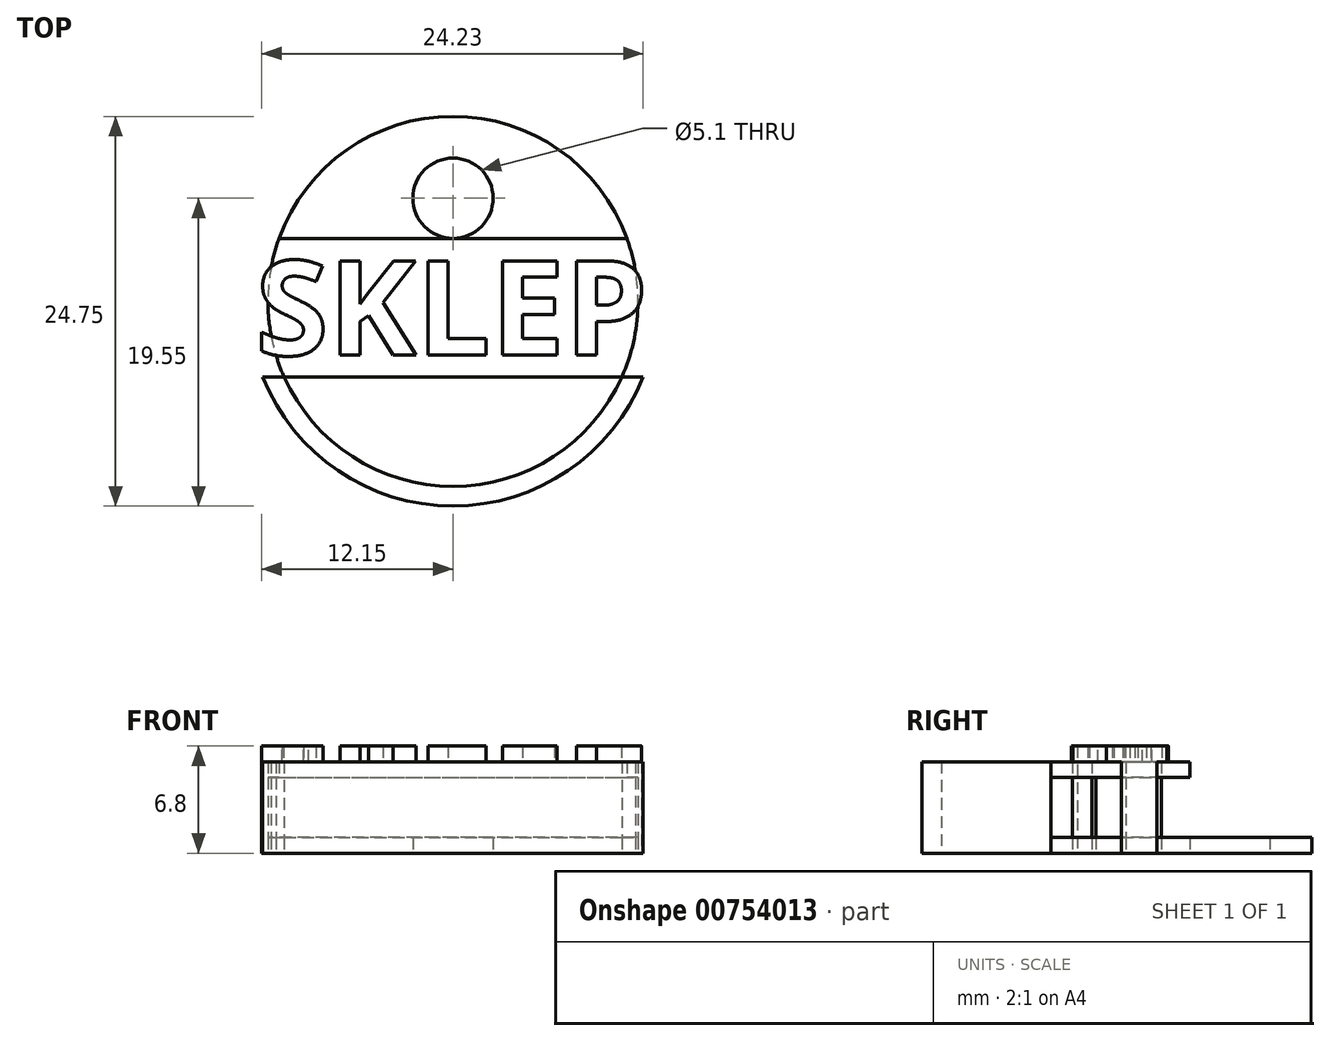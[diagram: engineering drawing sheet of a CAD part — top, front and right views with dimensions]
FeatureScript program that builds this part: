
annotation { "Feature Type Name" : "Feature", "Feature Type Description" : "" }
export const myFeature = defineFeature(function(context is Context, id is Id, definition is map)
    precondition{}
    {
        {
            var Q0;
            Q0=qCreatedBy(makeId("Top.planeOp"),FACE);
            var sketch = newSketch(context, id + "F0", { "sketchPlane" : qUnion([Q0])});
            skCircle(sketch, "E0", {"center": v(0, 0) * mm, "radius": 13 * mm});
            skLineSegment(sketch, "E1", {"start": v(-12.08, -4.8) * mm, "end": v(12.08, -4.8) * mm});
            skCircle(sketch, "E2", {"center": v(0, 6.55) * mm, "radius": 2.55 * mm});
            skCircle(sketch, "E3", {"center": v(0, 0) * mm, "radius": 11.75 * mm});
            skLineSegment(sketch, "E4", {"start": v(0, 4) * mm, "end": v(-11.05, 4) * mm});
            skLineSegment(sketch, "E5", {"start": v(0, 4) * mm, "end": v(11.05, 4) * mm});
            skText(sketch, "E6", { "text": "SKLEP", "fontName": "OpenSans-Bold.ttf"});
            const initialGuessF0  = {"E6": [-0.01254, -0.00342, 1, 0, 0.00604]};
            skSetInitialGuess(sketch, initialGuessF0);
            skSolve(sketch);
        }
        {
            var Q0;
            {var subQ0=sQuery(id+"F0.wireOp",EDGE,"E4");Q0=makeQuery(id+"F0.imprint","IMPRINT",FACE,{"disambiguationData":[TD([[makeQuery(id+"F0.imprint","IMPRINT",EDGE,{"derivedFrom":subQ0}),1.0]])]});}
            var Q1;
            {var subQ0=sQuery(id+"F0.wireOp",EDGE,"E1");var subQ1=sQuery(id+"F0.wireOp",EDGE,"E0");var subQ5=makeQuery(id+"F0.imprint","INTERSECT",VERTEX,{"disambiguationData":[OD(0.0)],"derivedFrom":[subQ1,subQ0]});Q1=makeQuery(id+"F0.imprint","IMPRINT",FACE,{"disambiguationData":[TD([[makeQuery(id+"F0.imprint","IMPRINT",EDGE,{"disambiguationData":[TD([[subQ5,1.0]])],"derivedFrom":subQ1}),1.0]])]});}
            var Q2;
            Q2=makeQuery(id+"F0.imprint","IMPRINT",FACE,{"disambiguationData":[TD([[makeQuery(id+"F0.imprint","IMPRINT",EDGE,{"derivedFrom":sQuery(id+"F0.wireOp",EDGE,"E6.sketch_text.stroke-59")}),1.0]])]});
            var Q3;
            {var subQ0=sQuery(id+"F0.wireOp",EDGE,"E6.sketch_text.stroke-5");Q3=makeQuery(id+"F0.imprint","IMPRINT",FACE,{"disambiguationData":[TD([[makeQuery(id+"F0.imprint","IMPRINT",EDGE,{"derivedFrom":subQ0}),1.0]])]});}
            extrude(context, id + "F1", {"entities" : qUnion([Q0, Q1, Q2, Q3]), "depth" : 5.8 * mm, "offsetDistance" : 25 * mm});
        }
        {
            var Q0;
            Q0=makeQuery(id+"F0.imprint","IMPRINT",FACE,{"disambiguationData":[TD([[makeQuery(id+"F0.imprint","IMPRINT",EDGE,{"derivedFrom":sQuery(id+"F0.wireOp",EDGE,"E6.sketch_text.stroke-41")}),-1.0]])]});
            var Q1;
            Q1=makeQuery(id+"F0.imprint","IMPRINT",FACE,{"disambiguationData":[TD([[makeQuery(id+"F0.imprint","IMPRINT",EDGE,{"derivedFrom":sQuery(id+"F0.wireOp",EDGE,"E6.sketch_text.stroke-47")}),-1.0]])]});
            var Q2;
            Q2=makeQuery(id+"F0.imprint","IMPRINT",FACE,{"disambiguationData":[TD([[makeQuery(id+"F0.imprint","IMPRINT",EDGE,{"derivedFrom":sQuery(id+"F0.wireOp",EDGE,"E6.sketch_text.stroke-59")}),-1.0]])]});
            var Q3;
            Q3=makeQuery(id+"F0.imprint","IMPRINT",FACE,{"disambiguationData":[TD([[makeQuery(id+"F0.imprint","IMPRINT",EDGE,{"derivedFrom":sQuery(id+"F0.wireOp",EDGE,"E6.sketch_text.stroke-28")}),-1.0]])]});
            var Q4;
            Q4=makeQuery(id+"F0.imprint","IMPRINT",FACE,{"disambiguationData":[TD([[makeQuery(id+"F0.imprint","IMPRINT",EDGE,{"derivedFrom":sQuery(id+"F0.wireOp",EDGE,"E6.sketch_text.stroke-0")}),-1.0]])]});
            var Q5;
            {var subQ5=sQuery(id+"F0.wireOp",EDGE,"E6.sketch_text.stroke-3");Q5=makeQuery(id+"F0.imprint","IMPRINT",FACE,{"disambiguationData":[TD([[makeQuery(id+"F0.imprint","IMPRINT",EDGE,{"derivedFrom":subQ5}),-1.0]])]});}
            var Q6;
            {var subQ1=sQuery(id+"F0.wireOp",EDGE,"E6.sketch_text.stroke-13");Q6=makeQuery(id+"F0.imprint","IMPRINT",FACE,{"disambiguationData":[TD([[makeQuery(id+"F0.imprint","IMPRINT",EDGE,{"derivedFrom":subQ1}),-1.0]])]});}
            var Q7;
            {var subQ5=sQuery(id+"F0.wireOp",EDGE,"E6.sketch_text.stroke-74");Q7=makeQuery(id+"F0.imprint","IMPRINT",FACE,{"disambiguationData":[TD([[makeQuery(id+"F0.imprint","IMPRINT",EDGE,{"derivedFrom":subQ5}),-1.0]])]});}
            extrude(context, id + "F2", {"entities" : qUnion([Q0, Q1, Q2, Q3, Q4, Q5, Q6, Q7]), "operationType" : NewBodyOperationType.ADD, "depth" : 6.8 * mm, "offsetDistance" : 25 * mm});
        }
        {
            var Q0;
            {var subQ0=sQuery(id+"F0.wireOp",EDGE,"E4");Q0=makeQuery(id+"F0.imprint","IMPRINT",FACE,{"disambiguationData":[TD([[makeQuery(id+"F0.imprint","IMPRINT",EDGE,{"derivedFrom":subQ0}),1.0]])]});}
            var Q1;
            Q1=makeQuery(id+"F0.imprint","IMPRINT",FACE,{"disambiguationData":[TD([[makeQuery(id+"F0.imprint","IMPRINT",EDGE,{"derivedFrom":sQuery(id+"F0.wireOp",EDGE,"E6.sketch_text.stroke-0")}),-1.0]])]});
            var Q2;
            Q2=makeQuery(id+"F0.imprint","IMPRINT",FACE,{"disambiguationData":[TD([[makeQuery(id+"F0.imprint","IMPRINT",EDGE,{"derivedFrom":sQuery(id+"F0.wireOp",EDGE,"E6.sketch_text.stroke-28")}),-1.0]])]});
            var Q3;
            Q3=makeQuery(id+"F0.imprint","IMPRINT",FACE,{"disambiguationData":[TD([[makeQuery(id+"F0.imprint","IMPRINT",EDGE,{"derivedFrom":sQuery(id+"F0.wireOp",EDGE,"E6.sketch_text.stroke-41")}),-1.0]])]});
            var Q4;
            Q4=makeQuery(id+"F0.imprint","IMPRINT",FACE,{"disambiguationData":[TD([[makeQuery(id+"F0.imprint","IMPRINT",EDGE,{"derivedFrom":sQuery(id+"F0.wireOp",EDGE,"E6.sketch_text.stroke-47")}),-1.0]])]});
            var Q5;
            Q5=makeQuery(id+"F0.imprint","IMPRINT",FACE,{"disambiguationData":[TD([[makeQuery(id+"F0.imprint","IMPRINT",EDGE,{"derivedFrom":sQuery(id+"F0.wireOp",EDGE,"E6.sketch_text.stroke-59")}),-1.0]])]});
            var Q6;
            Q6=makeQuery(id+"F0.imprint","IMPRINT",FACE,{"disambiguationData":[TD([[makeQuery(id+"F0.imprint","IMPRINT",EDGE,{"derivedFrom":sQuery(id+"F0.wireOp",EDGE,"E6.sketch_text.stroke-59")}),1.0]])]});
            var Q7;
            {var subQ0=sQuery(id+"F0.wireOp",EDGE,"E6.sketch_text.stroke-5");Q7=makeQuery(id+"F0.imprint","IMPRINT",FACE,{"disambiguationData":[TD([[makeQuery(id+"F0.imprint","IMPRINT",EDGE,{"derivedFrom":subQ0}),1.0]])]});}
            extrude(context, id + "F3", {"entities" : qUnion([Q0, Q1, Q2, Q3, Q4, Q5, Q6, Q7]), "operationType" : NewBodyOperationType.REMOVE, "depth" : 4.8 * mm, "offsetDistance" : 25 * mm});
        }
        {
            var Q0;
            Q0=makeQuery(id+"F0.imprint","IMPRINT",FACE,{"disambiguationData":[TD([[makeQuery(id+"F0.imprint","IMPRINT",EDGE,{"derivedFrom":sQuery(id+"F0.wireOp",EDGE,"E2")}),-1.0]])]});
            var Q1;
            {var subQ0=sQuery(id+"F0.wireOp",EDGE,"E4");Q1=makeQuery(id+"F0.imprint","IMPRINT",FACE,{"disambiguationData":[TD([[makeQuery(id+"F0.imprint","IMPRINT",EDGE,{"derivedFrom":subQ0}),1.0]])]});}
            var Q2;
            Q2=makeQuery(id+"F0.imprint","IMPRINT",FACE,{"disambiguationData":[TD([[makeQuery(id+"F0.imprint","IMPRINT",EDGE,{"derivedFrom":sQuery(id+"F0.wireOp",EDGE,"E6.sketch_text.stroke-0")}),-1.0]])]});
            var Q3;
            Q3=makeQuery(id+"F0.imprint","IMPRINT",FACE,{"disambiguationData":[TD([[makeQuery(id+"F0.imprint","IMPRINT",EDGE,{"derivedFrom":sQuery(id+"F0.wireOp",EDGE,"E6.sketch_text.stroke-28")}),-1.0]])]});
            var Q4;
            Q4=makeQuery(id+"F0.imprint","IMPRINT",FACE,{"disambiguationData":[TD([[makeQuery(id+"F0.imprint","IMPRINT",EDGE,{"derivedFrom":sQuery(id+"F0.wireOp",EDGE,"E6.sketch_text.stroke-41")}),-1.0]])]});
            var Q5;
            Q5=makeQuery(id+"F0.imprint","IMPRINT",FACE,{"disambiguationData":[TD([[makeQuery(id+"F0.imprint","IMPRINT",EDGE,{"derivedFrom":sQuery(id+"F0.wireOp",EDGE,"E6.sketch_text.stroke-47")}),-1.0]])]});
            var Q6;
            Q6=makeQuery(id+"F0.imprint","IMPRINT",FACE,{"disambiguationData":[TD([[makeQuery(id+"F0.imprint","IMPRINT",EDGE,{"derivedFrom":sQuery(id+"F0.wireOp",EDGE,"E6.sketch_text.stroke-59")}),-1.0]])]});
            var Q7;
            Q7=makeQuery(id+"F0.imprint","IMPRINT",FACE,{"disambiguationData":[TD([[makeQuery(id+"F0.imprint","IMPRINT",EDGE,{"derivedFrom":sQuery(id+"F0.wireOp",EDGE,"E6.sketch_text.stroke-59")}),1.0]])]});
            var Q8;
            {var subQ0=sQuery(id+"F0.wireOp",EDGE,"E6.sketch_text.stroke-5");Q8=makeQuery(id+"F0.imprint","IMPRINT",FACE,{"disambiguationData":[TD([[makeQuery(id+"F0.imprint","IMPRINT",EDGE,{"derivedFrom":subQ0}),1.0]])]});}
            extrude(context, id + "F4", {"entities" : qUnion([Q0, Q1, Q2, Q3, Q4, Q5, Q6, Q7, Q8]), "operationType" : NewBodyOperationType.ADD, "depth" : 1 * mm, "offsetDistance" : 25 * mm});
        }
    });
